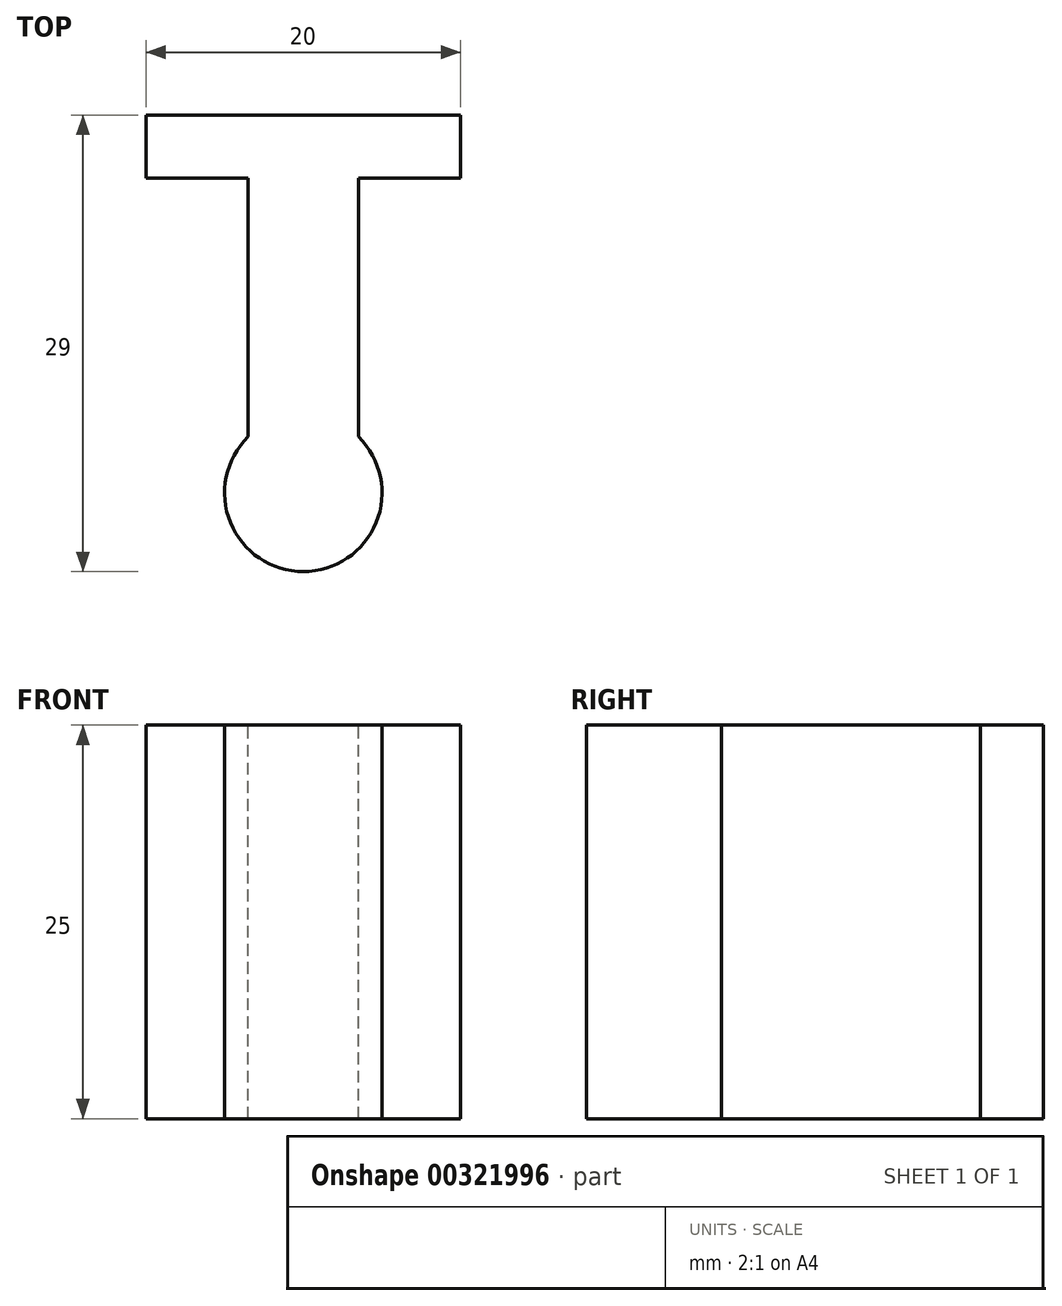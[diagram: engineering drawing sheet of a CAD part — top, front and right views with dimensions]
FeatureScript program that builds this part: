
annotation { "Feature Type Name" : "Feature", "Feature Type Description" : "" }
export const myFeature = defineFeature(function(context is Context, id is Id, definition is map)
    precondition{}
    {
        {
            var Q0;
            Q0=qCreatedBy(makeId("Top.planeOp"),FACE);
            var sketch = newSketch(context, id + "F0", { "sketchPlane" : qUnion([Q0])});
            skArc(sketch, "E0", {"start": v(-3.5, 3.57) * mm, "mid": v(0, -5) * mm, "end": v(3.5, 3.57) * mm});
            skLineSegment(sketch, "E1.left", {"start": v(-3.5, 3.57) * mm, "end": v(-3.5, 20) * mm});
            skLineSegment(sketch, "E1.right", {"start": v(3.5, 3.57) * mm, "end": v(3.5, 20) * mm});
            skLineSegment(sketch, "E2.bottom", {"start": v(-10, 24) * mm, "end": v(10, 24) * mm});
            skLineSegment(sketch, "E2.top", {"start": v(-10, 20) * mm, "end": v(-3.5, 20) * mm});
            skLineSegment(sketch, "E2.left", {"start": v(-10, 24) * mm, "end": v(-10, 20) * mm});
            skLineSegment(sketch, "E2.right", {"start": v(10, 24) * mm, "end": v(10, 20) * mm});
            skLineSegment(sketch, "E3.trimOffspring", {"start": v(3.5, 20) * mm, "end": v(10, 20) * mm});
            skSolve(sketch);
        }
        {
            var Q0;
            Q0=makeQuery(id+"F0.imprint","IMPRINT",FACE,{"disambiguationData":[TD([[makeQuery(id+"F0.imprint","IMPRINT",EDGE,{"derivedFrom":sQuery(id+"F0.wireOp",EDGE,"E0")}),1.0]])]});
            extrude(context, id + "F1", {"entities" : qUnion([Q0]), "oppositeDirection" : true, "depth" : 25 * mm});
        }
    });
